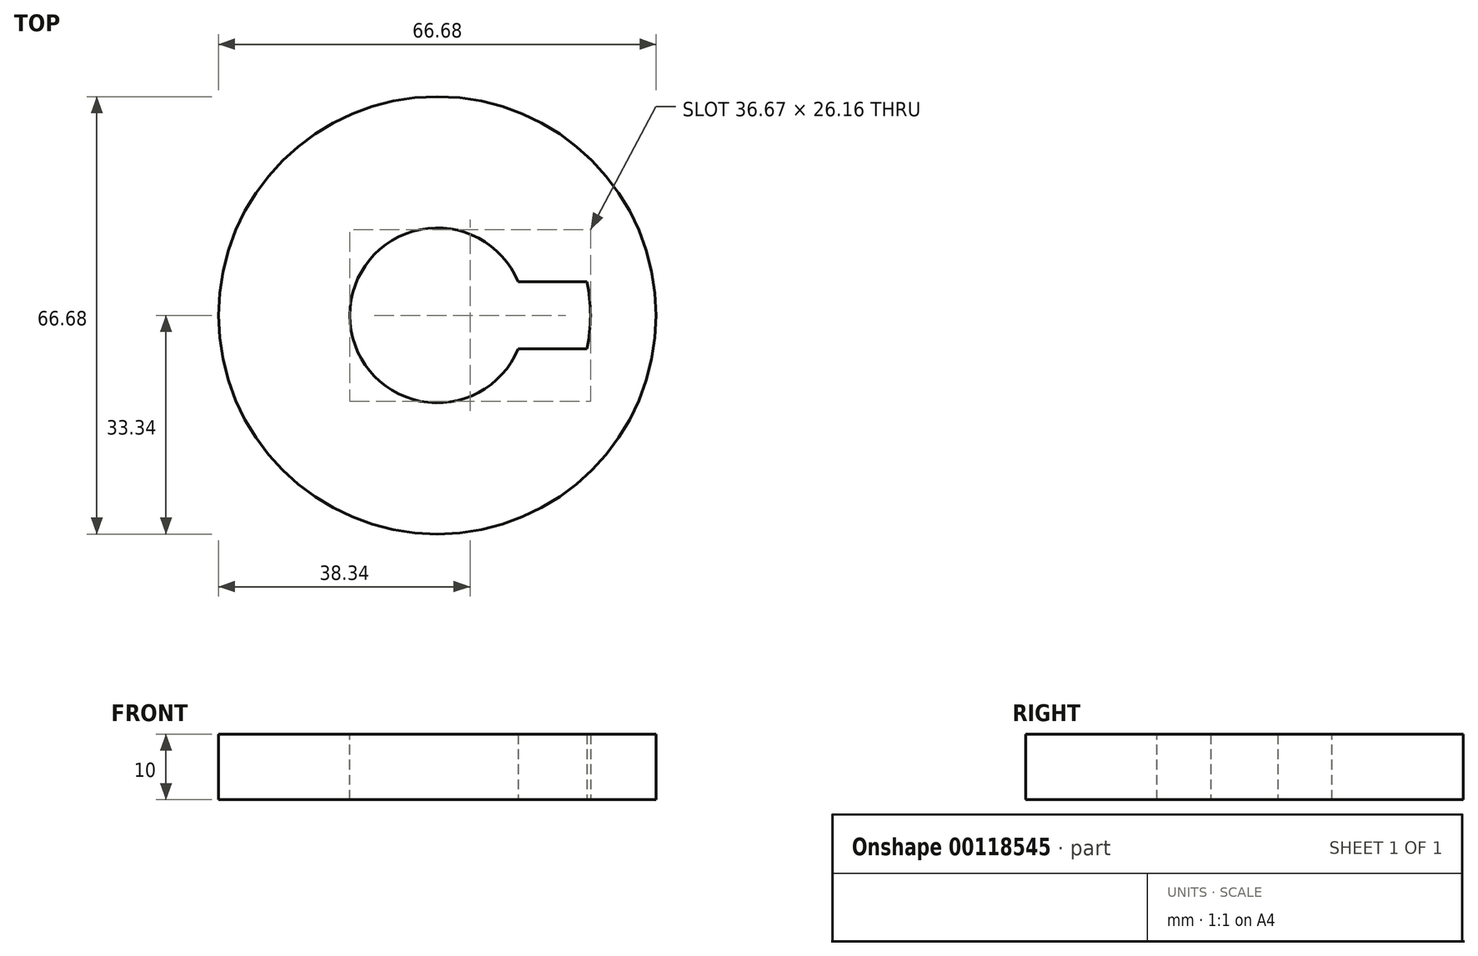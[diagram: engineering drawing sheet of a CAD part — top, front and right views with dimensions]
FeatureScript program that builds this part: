
annotation { "Feature Type Name" : "Feature", "Feature Type Description" : "" }
export const myFeature = defineFeature(function(context is Context, id is Id, definition is map)
    precondition{}
    {
        {
            var Q0;
            Q0=qCreatedBy(makeId("Top.planeOp"),FACE);
            var sketch = newSketch(context, id + "F0", { "sketchPlane" : qUnion([Q0])});
            skCircle(sketch, "E0", {"center": v(0, 0) * mm, "radius": 13.34 * mm, "construction": true});
            skCircle(sketch, "E1", {"center": v(0, 0) * mm, "radius": 23.34 * mm, "construction": true});
            skCircle(sketch, "E2", {"center": v(0, 0) * mm, "radius": 33.34 * mm});
            skSolve(sketch);
        }
        {
            var Q0;
            Q0=makeQuery(id+"F0.imprint","IMPRINT",FACE,{"disambiguationData":[TD([[makeQuery(id+"F0.imprint","IMPRINT",EDGE,{"derivedFrom":sQuery(id+"F0.wireOp",EDGE,"E2")}),1.0]])]});
            extrude(context, id + "F1", {"entities" : qUnion([Q0]), "depth" : 10 * mm});
        }
        {
            var Q0;
            Q0=makeQuery(id+"F1.opExtrude","CAP_FACE",FACE,{"disambiguationData":[OSD([sQuery(id+"F0.wireOp",EDGE,"E2")])],"isStart":false});
            var sketch = newSketch(context, id + "F2", { "sketchPlane" : qUnion([Q0])});
            skCircle(sketch, "E3", {"center": v(0, 0) * mm, "radius": 13.33 * mm});
            skSolve(sketch);
        }
        {
            var Q0;
            Q0=makeQuery(id+"F2.imprint","IMPRINT",FACE,{"disambiguationData":[TD([[makeQuery(id+"F2.imprint","IMPRINT",EDGE,{"derivedFrom":sQuery(id+"F2.wireOp",EDGE,"E3")}),1.0]])]});
            extrude(context, id + "F3", {"entities" : qUnion([Q0]), "operationType" : NewBodyOperationType.REMOVE, "endBound" : BoundingType.UP_TO_NEXT, "oppositeDirection" : true, "depth" : 25.4 * mm});
        }
        {
            var Q0;
            Q0=qCreatedBy(makeId("Top.planeOp"),FACE);
            var sketch = newSketch(context, id + "F4", { "sketchPlane" : qUnion([Q0])});
            skLineSegment(sketch, "E4", {"start": v(0, 0) * mm, "end": v(41.7, 17.28) * mm, "construction": true});
            skLineSegment(sketch, "E5", {"start": v(0, 0) * mm, "end": v(41.78, -17.3) * mm, "construction": true});
            skArc(sketch, "E6", {"start": v(12.32, 5.1) * mm, "mid": v(13.33, 0) * mm, "end": v(12.32, -5.1) * mm});
            skArc(sketch, "E7", {"start": v(22.77, 5.1) * mm, "mid": v(23.34, 0) * mm, "end": v(22.77, -5.1) * mm});
            skLineSegment(sketch, "E8", {"start": v(12.32, 5.1) * mm, "end": v(22.77, 5.1) * mm});
            skLineSegment(sketch, "E9", {"start": v(12.32, -5.1) * mm, "end": v(22.77, -5.1) * mm});
            skSolve(sketch);
        }
        {
            var Q0;
            Q0 = qSketchRegion(id + "F4", true);
            extrude(context, id + "F5", {"entities" : qUnion([Q0]), "operationType" : NewBodyOperationType.REMOVE, "endBound" : BoundingType.UP_TO_NEXT, "depth" : 10 * mm, "offsetDistance" : 25.4 * mm});
        }
    });
